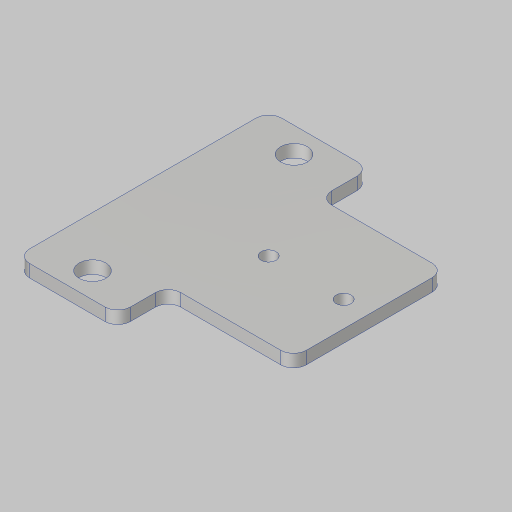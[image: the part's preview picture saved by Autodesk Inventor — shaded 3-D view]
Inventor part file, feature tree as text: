
AUTODESK INVENTOR PART (.ipt)
format: ipt  version: 2023.5 (Build 275446000, 446)  size: 130,048 bytes
history: native  units: in
note: dims shown in document units (in); Inventor stores cm internally (conversion verified against a paired STEP export)
features: sketch x3, hole x2, extrude x1, fillet x1
ambient origin geometry x8: Origin, YZ Plane, XZ Plane, XY Plane, X Axis, Y Axis, Z Axis, Center Point
bodies: Solid1 (feature_tree)
feature tree (7):
  extrude  "Extrusion1"  Depth=2.5in
  hole  "Hole1"  [1 undecoded]
  hole  "Hole2"  [1 undecoded]
  fillet  "Fillet1"  Radius=1.245in
  sketch  "Sketch1"  dims[d0=1.0in d1=2.5in]
  sketch  "Sketch2"  dims[d2=0.125in d3=0.0in d4=2.0in]
  sketch  "Sketch3"  dims[d6=0.266in d7=0.432in d8=0.119in d9=0.25in d10=0.5635in d11=1.0in d12=0.8108in d13=0.7447in d14=0.15in d15=0.75in d16=0.279in d17=0.25in d18=0.5635in d19=1.0in d20=0.8108in d21=1.245in d22=0.5in d23=0.5in d24=0.253in d25=0.125in]
note: 2 required parameter values undecoded (feature->parameter linkage not recoverable at this tier; creation-order binding heuristic only, values carry confidence <= 0.55)
